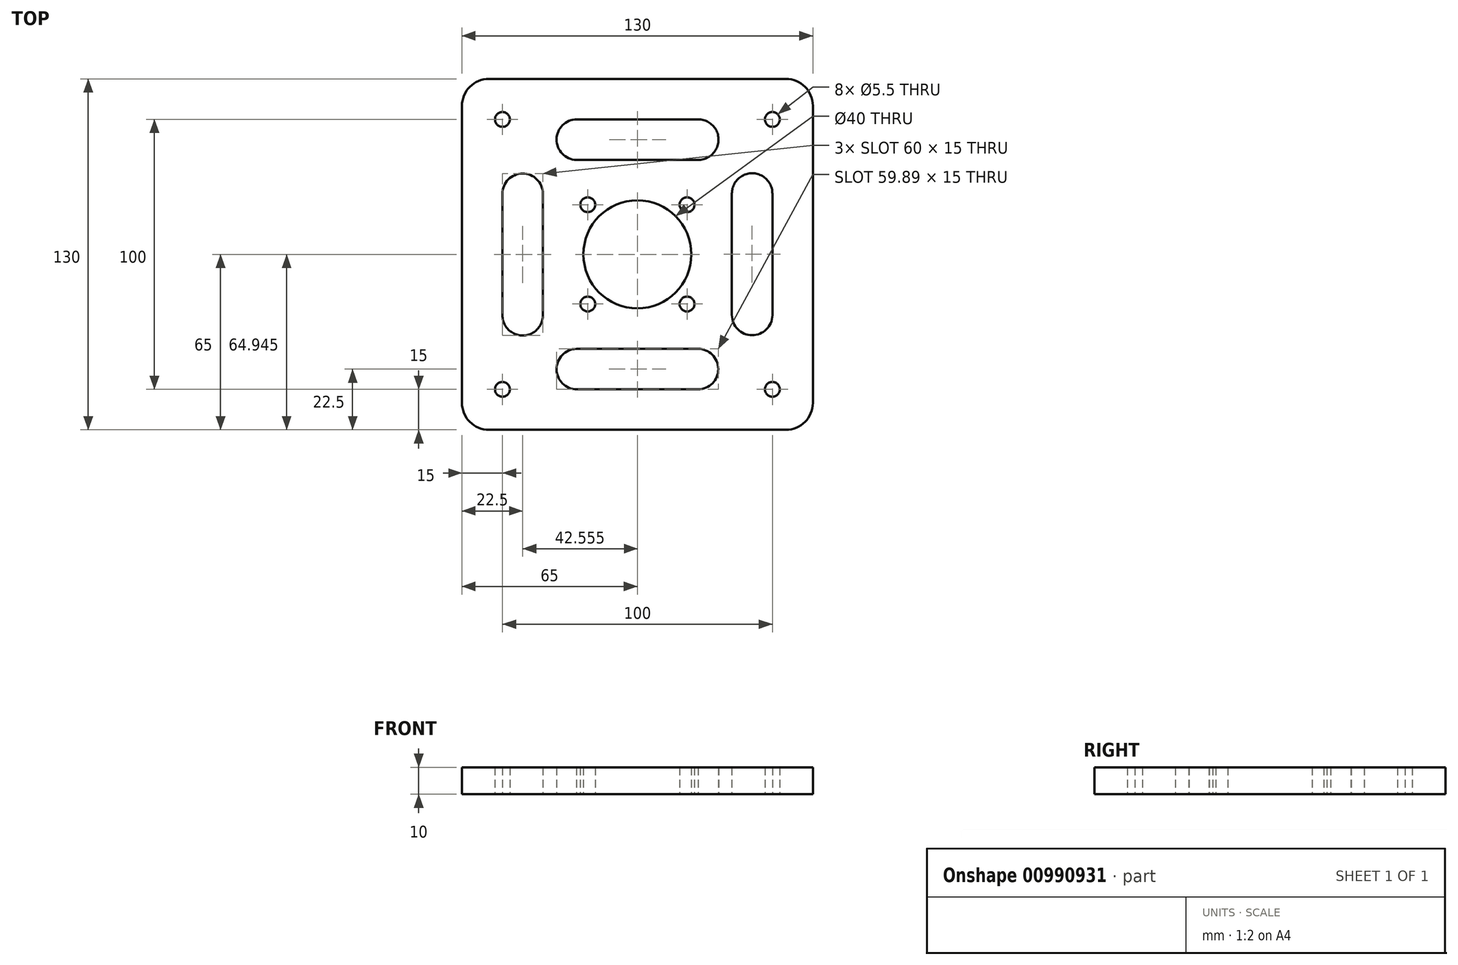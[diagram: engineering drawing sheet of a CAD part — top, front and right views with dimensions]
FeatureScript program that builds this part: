
annotation { "Feature Type Name" : "Feature", "Feature Type Description" : "" }
export const myFeature = defineFeature(function(context is Context, id is Id, definition is map)
    precondition{}
    {
        {
            var Q0;
            Q0=qCreatedBy(makeId("Top.planeOp"),FACE);
            var sketch = newSketch(context, id + "F0", { "sketchPlane" : qUnion([Q0])});
            skLineSegment(sketch, "E0.bottom", {"start": v(55, -65) * mm, "end": v(-55, -65) * mm});
            skLineSegment(sketch, "E0.top", {"start": v(55, 65) * mm, "end": v(-55, 65) * mm});
            skLineSegment(sketch, "E0.left", {"start": v(65, -55) * mm, "end": v(65, 55) * mm});
            skLineSegment(sketch, "E0.right", {"start": v(-65, -55) * mm, "end": v(-65, 55) * mm});
            skPoint(sketch, "E0.middle", {"position": v(0, 0) * mm});
            skCircle(sketch, "E1", {"center": v(0, 0) * mm, "radius": 20 * mm});
            skLineSegment(sketch, "E2", {"start": v(20, 0) * mm, "end": v(65, 0) * mm, "construction": true});
            skLineSegment(sketch, "E3", {"start": v(0, -20) * mm, "end": v(0, -65) * mm, "construction": true});
            skCircle(sketch, "E4", {"center": v(-50, 50) * mm, "radius": 2.75 * mm});
            skCircle(sketch, "E5.MirrorC", {"center": v(50, 50) * mm, "radius": 2.75 * mm});
            skCircle(sketch, "E6.MirrorC", {"center": v(-50, -50) * mm, "radius": 2.75 * mm});
            skCircle(sketch, "E7.MirrorC", {"center": v(50, -50) * mm, "radius": 2.75 * mm});
            skCircle(sketch, "E8", {"center": v(-18.38, 18.38) * mm, "radius": 2.75 * mm});
            skCircle(sketch, "E9.MirrorC", {"center": v(18.38, 18.38) * mm, "radius": 2.75 * mm});
            skCircle(sketch, "E10.MirrorC", {"center": v(-18.38, -18.38) * mm, "radius": 2.75 * mm});
            skCircle(sketch, "E11.MirrorC", {"center": v(18.38, -18.38) * mm, "radius": 2.75 * mm});
            skCircle(sketch, "E12", {"center": v(0, 0) * mm, "radius": 26 * mm, "construction": true});
            skLineSegment(sketch, "E13.left", {"start": v(-35, -22.45) * mm, "end": v(-35, 22.55) * mm});
            skLineSegment(sketch, "E13.right", {"start": v(-50, -22.55) * mm, "end": v(-50, 22.45) * mm});
            skPoint(sketch, "E13.middle", {"position": v(-42.5, 0) * mm});
            skLineSegment(sketch, "E14.MirrorCS", {"start": v(50, -22.55) * mm, "end": v(50, 22.45) * mm});
            skLineSegment(sketch, "E15.MirrorCS", {"start": v(35, -22.45) * mm, "end": v(35, 22.55) * mm});
            skLineSegment(sketch, "E16", {"start": v(-65, 65) * mm, "end": v(65, -65) * mm, "construction": true});
            skLineSegment(sketch, "E17.MirrorCS", {"start": v(22.45, -35) * mm, "end": v(-22.55, -35) * mm});
            skLineSegment(sketch, "E18.MirrorCS", {"start": v(22.55, -50) * mm, "end": v(-22.45, -50) * mm});
            skLineSegment(sketch, "E19.MirrorCS", {"start": v(22.45, 35) * mm, "end": v(-22.55, 35) * mm});
            skLineSegment(sketch, "E20.MirrorCS", {"start": v(22.55, 50) * mm, "end": v(-22.45, 50) * mm});
            skPoint(sketch, "E21.visualSharp", {"position": v(-65, 65) * mm});
            skArc(sketch, "E21.filletArc", {"start": v(-55, 65) * mm, "mid": v(-62.07, 62.07) * mm, "end": v(-65, 55) * mm});
            skPoint(sketch, "E22.visualSharp", {"position": v(65, 65) * mm});
            skArc(sketch, "E22.filletArc", {"start": v(65, 55) * mm, "mid": v(62.07, 62.07) * mm, "end": v(55, 65) * mm});
            skPoint(sketch, "E23.visualSharp", {"position": v(-65, -65) * mm});
            skArc(sketch, "E23.filletArc", {"start": v(-65, -55) * mm, "mid": v(-62.07, -62.07) * mm, "end": v(-55, -65) * mm});
            skPoint(sketch, "E24.visualSharp", {"position": v(65, -65) * mm});
            skArc(sketch, "E24.filletArc", {"start": v(55, -65) * mm, "mid": v(62.07, -62.07) * mm, "end": v(65, -55) * mm});
            skArc(sketch, "E25", {"start": v(-35, 22.55) * mm, "mid": v(-42.55, 29.95) * mm, "end": v(-50, 22.45) * mm});
            skArc(sketch, "E26", {"start": v(-50, -22.55) * mm, "mid": v(-42.44, -30.06) * mm, "end": v(-35, -22.45) * mm});
            skArc(sketch, "E27", {"start": v(-22.55, -35) * mm, "mid": v(-29.95, -42.55) * mm, "end": v(-22.45, -50) * mm});
            skArc(sketch, "E28", {"start": v(22.55, -50) * mm, "mid": v(29.95, -42.45) * mm, "end": v(22.45, -35) * mm});
            skArc(sketch, "E29", {"start": v(35, -22.45) * mm, "mid": v(42.45, -29.95) * mm, "end": v(50, -22.55) * mm});
            skArc(sketch, "E30", {"start": v(50, 22.45) * mm, "mid": v(42.56, 30.06) * mm, "end": v(35, 22.55) * mm});
            skArc(sketch, "E31", {"start": v(22.45, 35) * mm, "mid": v(30.06, 42.44) * mm, "end": v(22.55, 50) * mm});
            skArc(sketch, "E32", {"start": v(-22.45, 50) * mm, "mid": v(-29.95, 42.55) * mm, "end": v(-22.55, 35) * mm});
            skPoint(sketch, "E33.orphan", {"position": v(-22.55, -35) * mm});
            skPoint(sketch, "E34.orphan", {"position": v(22.45, -35) * mm});
            skPoint(sketch, "E35.orphan", {"position": v(50, -22.55) * mm});
            skPoint(sketch, "E36.MirrorCS.start.orphan", {"position": v(35, -22.45) * mm});
            skPoint(sketch, "E37.orphan", {"position": v(22.55, 50) * mm});
            skPoint(sketch, "E38.MirrorCS.start.orphan", {"position": v(22.45, 35) * mm});
            skPoint(sketch, "E39.orphan", {"position": v(-22.45, 50) * mm});
            skPoint(sketch, "E40.MirrorCS.start.orphan", {"position": v(-22.55, 35) * mm});
            skLineSegment(sketch, "E41", {"start": v(65, 65) * mm, "end": v(-65, -65) * mm, "construction": true});
            skSolve(sketch);
        }
        {
            var Q0;
            Q0 = qSketchRegion(id + "F0", true);
            extrude(context, id + "F1", {"entities" : qUnion([Q0]), "depth" : 10 * mm, "offsetDistance" : 25 * mm});
        }
    });
